# Revit family: Sanitary_Taps-Mixers_hansgrohe_Isiflex-Shower-hose-160-cm-28276000_NEW
name_source: partatom
category: Plumbing Fixtures
revit_build: Autodesk Revit 2015 (Build: 20140903_1530(x64)
units: mm (PartAtom-declared; Revit-internal decimal feet)

## types (2) — shared parameters
Always visible = Yes
BIMobject category = Taps & Mixers
BIMobject category code = sanitary-taps-mixers
BIMobject main category = Sanitary
BIMobject main category code = sanitary
Brand url = http://www.hansgrohe-int.com
Date of publishing = 3/26/2019
Design country = Germany
Edition number = 1
GTIN code = https://4011097314037
IFC Classification = Sanitary Terminal
Installation instructions = https://www.hansgrohe.com
Manufacturer country = Germany
Manufacturer name = hansgrohe
Masterformat 2014 Code = 22 41 23
Masterformat 2014 Description = Residential Showers
Material main = Chrome
NBS Reference Code = 35-06-82
NBS Reference Description = Shower Mixers
OmniClass Code = 23-31 11 00
OmniClass Description = Faucets
Product Guid = 703efe03-8739-4987-b28a-4b6cd80f6212
Product SKU = 28276000
Product data url = https://bimobject.com
Product family = Isiflex
Product group = Shower hoses
Product name = Isiflex Shower hose 160 cm 28276000
Product url = https://www.hansgrohe.com
QR code = http://bimobject.com
Technical description = https://www.hansgrohe.com
UNSPSC Code = 30181503
Uniclass 1.4 Code = L725111
Uniclass 1.4 Description = Mixer taps
Uniclass 2.0 Code = PR-35-06-82
Uniclass 2.0 Description = Shower Mixers
Uniclass 2015 Code = Pr_40_20_87_09
Uniclass 2015 Name = Bath taps
Uniformat II Code = D2010
Uniformat II Description = Plumbing Fixtures

## per-type parameters (varying)
| type | Material 1 |
| 700 Matt White | Hansgrohe - Isiflex - 700 Matt White |
| 000 Chrome | Hansgrohe - Isiflex - 000 Chrome |

## geometry (parser evidence)
native form markers: Sweep x2
no freeform markers — native parametric forms only
